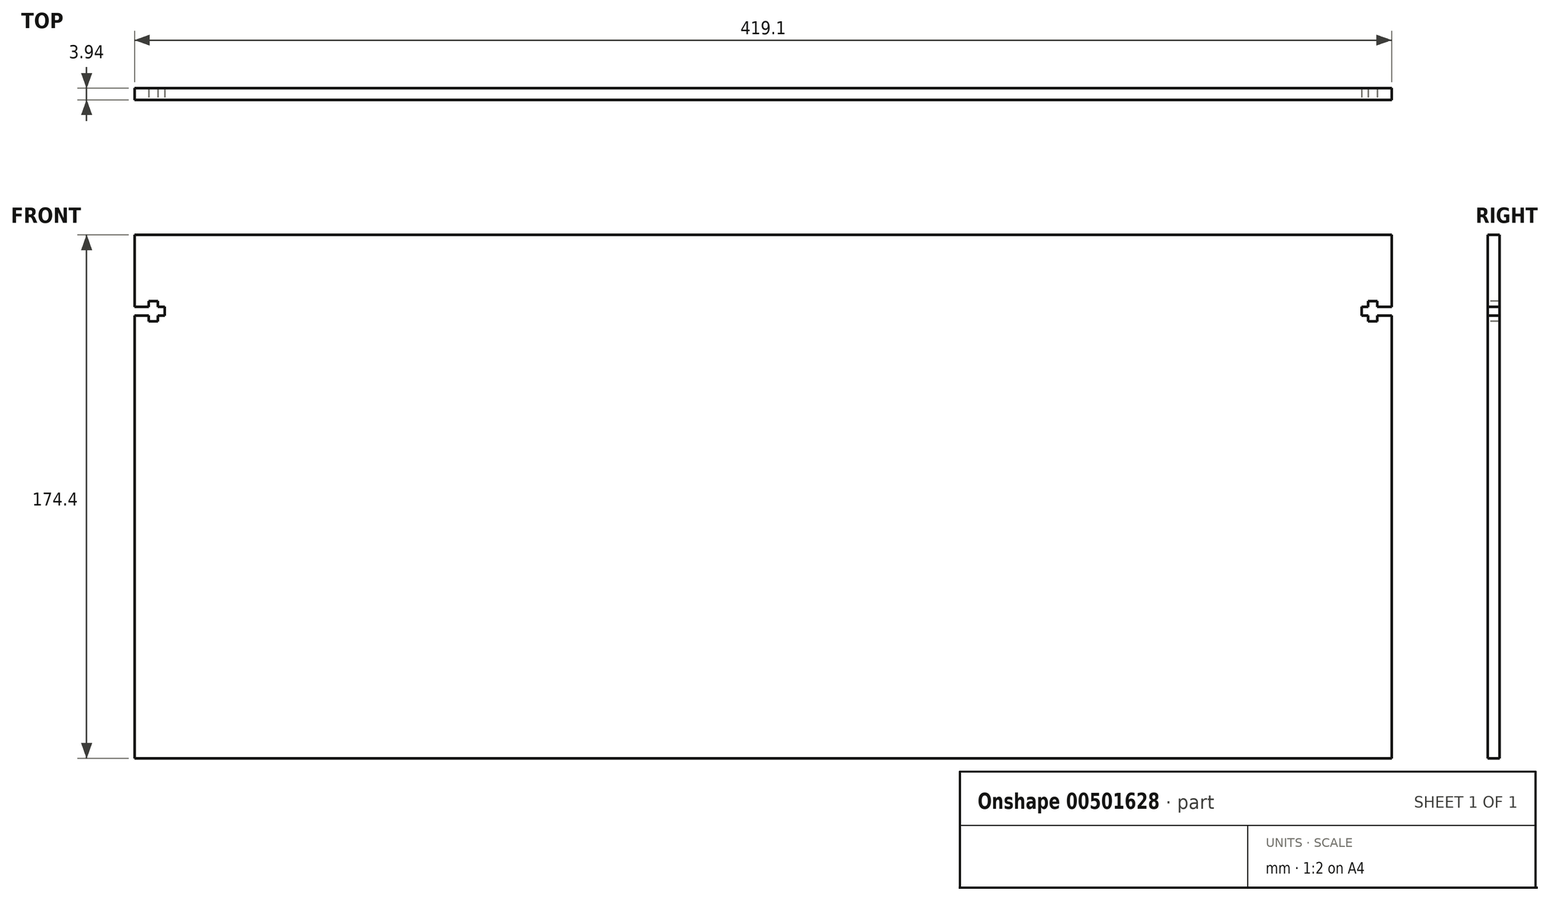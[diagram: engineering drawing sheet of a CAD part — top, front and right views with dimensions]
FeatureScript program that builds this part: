
annotation { "Feature Type Name" : "Feature", "Feature Type Description" : "" }
export const myFeature = defineFeature(function(context is Context, id is Id, definition is map)
    precondition{}
    {
        {
            var Q0;
            Q0=qCreatedBy(makeId("Front.planeOp"),FACE);
            var sketch = newSketch(context, id + "F0", { "sketchPlane" : qUnion([Q0])});
            skLineSegment(sketch, "E0.bottom", {"start": v(-209.55, 87.2) * mm, "end": v(209.55, 87.2) * mm});
            skLineSegment(sketch, "E0.top", {"start": v(-209.55, -87.2) * mm, "end": v(209.55, -87.2) * mm});
            skLineSegment(sketch, "E0.left", {"start": v(-209.55, 87.2) * mm, "end": v(-209.55, -87.2) * mm});
            skLineSegment(sketch, "E0.right", {"start": v(209.55, 87.2) * mm, "end": v(209.55, -87.2) * mm});
            skPoint(sketch, "E0.middle", {"position": v(0, 0) * mm});
            skSolve(sketch);
        }
        {
            var Q0;
            Q0=makeQuery(id+"F0.imprint","IMPRINT",FACE,{"disambiguationData":[TD([[makeQuery(id+"F0.imprint","IMPRINT",EDGE,{"derivedFrom":sQuery(id+"F0.wireOp",EDGE,"E0.bottom")}),-1.0]])]});
            extrude(context, id + "F1", {"entities" : qUnion([Q0]), "depth" : 3.94 * mm});
        }
        {
            var Q0;
            Q0=makeQuery(id+"F1.opExtrude","CAP_FACE",FACE,{"disambiguationData":[OSD([sQuery(id+"F0.wireOp",EDGE,"E0.bottom"),sQuery(id+"F0.wireOp",EDGE,"E0.top"),sQuery(id+"F0.wireOp",EDGE,"E0.left"),sQuery(id+"F0.wireOp",EDGE,"E0.right")])],"isStart":false});
            var sketch = newSketch(context, id + "F2", { "sketchPlane" : qUnion([Q0])});
            skLineSegment(sketch, "E1", {"start": v(-206.37, 61.8) * mm, "end": v(-199.52, 61.8) * mm, "construction": true});
            skLineSegment(sketch, "E2", {"start": v(-206.37, 60.32) * mm, "end": v(-204.77, 60.32) * mm});
            skLineSegment(sketch, "E3", {"start": v(-204.77, 60.32) * mm, "end": v(-204.77, 58.46) * mm});
            skLineSegment(sketch, "E4", {"start": v(-204.77, 58.46) * mm, "end": v(-201.74, 58.46) * mm});
            skLineSegment(sketch, "E5", {"start": v(-201.74, 58.46) * mm, "end": v(-201.74, 60.32) * mm});
            skLineSegment(sketch, "E6", {"start": v(-201.74, 60.32) * mm, "end": v(-199.52, 60.32) * mm});
            skLineSegment(sketch, "E7", {"start": v(-199.52, 60.32) * mm, "end": v(-199.52, 61.8) * mm});
            skLineSegment(sketch, "E8.MirrorCS", {"start": v(-204.77, 65.13) * mm, "end": v(-201.74, 65.13) * mm});
            skLineSegment(sketch, "E9.MirrorCS", {"start": v(-204.77, 63.27) * mm, "end": v(-204.77, 65.13) * mm});
            skLineSegment(sketch, "E10.MirrorCS", {"start": v(-206.37, 63.27) * mm, "end": v(-204.77, 63.27) * mm});
            skLineSegment(sketch, "E11.MirrorCS", {"start": v(-201.74, 65.13) * mm, "end": v(-201.74, 63.27) * mm});
            skLineSegment(sketch, "E12.MirrorCS", {"start": v(-201.74, 63.27) * mm, "end": v(-199.52, 63.27) * mm});
            skLineSegment(sketch, "E13.MirrorCS", {"start": v(-199.52, 63.27) * mm, "end": v(-199.52, 61.8) * mm});
            skLineSegment(sketch, "E14", {"start": v(-206.37, 63.27) * mm, "end": v(-206.37, 60.32) * mm});
            skLineSegment(sketch, "E15.bottom", {"start": v(-206.37, 63.27) * mm, "end": v(-209.55, 63.27) * mm});
            skLineSegment(sketch, "E15.top", {"start": v(-206.37, 60.32) * mm, "end": v(-209.55, 60.32) * mm});
            skLineSegment(sketch, "E15.right", {"start": v(-209.55, 63.27) * mm, "end": v(-209.55, 60.32) * mm});
            skLineSegment(sketch, "E16.MirrorCS", {"start": v(204.77, 58.46) * mm, "end": v(201.74, 58.46) * mm});
            skLineSegment(sketch, "E17.MirrorCS", {"start": v(206.37, 63.27) * mm, "end": v(206.37, 60.32) * mm});
            skLineSegment(sketch, "E18.MirrorCS", {"start": v(199.52, 63.27) * mm, "end": v(199.52, 61.8) * mm});
            skLineSegment(sketch, "E19.MirrorCS", {"start": v(201.74, 60.32) * mm, "end": v(199.52, 60.32) * mm});
            skLineSegment(sketch, "E20.MirrorCS", {"start": v(206.37, 60.32) * mm, "end": v(204.77, 60.32) * mm});
            skLineSegment(sketch, "E21.MirrorCS", {"start": v(201.74, 58.46) * mm, "end": v(201.74, 60.32) * mm});
            skLineSegment(sketch, "E22.MirrorCS", {"start": v(204.77, 63.27) * mm, "end": v(204.77, 65.13) * mm});
            skLineSegment(sketch, "E23.MirrorCS", {"start": v(204.77, 65.13) * mm, "end": v(201.74, 65.13) * mm});
            skLineSegment(sketch, "E24.MirrorCS", {"start": v(199.52, 60.32) * mm, "end": v(199.52, 61.8) * mm});
            skLineSegment(sketch, "E25.MirrorCS", {"start": v(206.37, 60.33) * mm, "end": v(209.55, 60.33) * mm});
            skLineSegment(sketch, "E26.MirrorCS", {"start": v(206.37, 63.27) * mm, "end": v(209.55, 63.27) * mm});
            skLineSegment(sketch, "E27.MirrorCS", {"start": v(201.74, 65.13) * mm, "end": v(201.74, 63.27) * mm});
            skLineSegment(sketch, "E28.MirrorCS", {"start": v(204.77, 60.32) * mm, "end": v(204.77, 58.46) * mm});
            skLineSegment(sketch, "E29.MirrorCS", {"start": v(206.37, 63.27) * mm, "end": v(204.77, 63.27) * mm});
            skLineSegment(sketch, "E30.MirrorCS", {"start": v(209.55, 63.27) * mm, "end": v(209.55, 60.32) * mm});
            skLineSegment(sketch, "E31.MirrorCS", {"start": v(206.37, 61.8) * mm, "end": v(199.52, 61.8) * mm, "construction": true});
            skLineSegment(sketch, "E32.MirrorCS", {"start": v(201.74, 63.27) * mm, "end": v(199.52, 63.27) * mm});
            skSolve(sketch);
        }
        {
            var Q0;
            Q0=qSketchRegion(id+"F2",true);
            var Q1;
            Q1=makeQuery(id+"F1.opExtrude","CAP_FACE",FACE,{"disambiguationData":[OSD([sQuery(id+"F0.wireOp",EDGE,"E0.bottom"),sQuery(id+"F0.wireOp",EDGE,"E0.top"),sQuery(id+"F0.wireOp",EDGE,"E0.left"),sQuery(id+"F0.wireOp",EDGE,"E0.right")])],"isStart":true});
            extrude(context, id + "F3", {"entities" : qUnion([Q0]), "operationType" : NewBodyOperationType.REMOVE, "endBound" : BoundingType.UP_TO_SURFACE, "oppositeDirection" : true, "endBoundEntityFace" : qUnion([Q1]), "depth" : 25.4 * mm});
        }
    });
